# Revit family: Roller_Shades-Lutron-Wall_Mount-Roller_64
name_source: partatom
category: Specialty Equipment
revit_build: Autodesk Revit 2017 (Build: 20160720_1515(x64)
units: mm (PartAtom-declared; Revit-internal decimal feet)

## family parameters
Cut with Voids When Loaded = No
Host = Face
OmniClass Number = 23.30.60.14.21
OmniClass Title = Shades
Part Type = Normal
Room Calculation Point = No
Round Connector Dimension = Use Diameter
Shared = No

## types (4) — shared parameters
Assembly Code = E2010320
Default Elevation = 9' - 0"
Description = Motorized Roller Shade
Fabric Roll Detail = Standard
Instruction Sheet Link = http://www.lutron.com
Manufacturer = Lutron Electronics Co., Inc
Manufacturer Fax Number = 610-282-1243
Maximum Shade Area = 64.00 SF
Model = Roller 64
Performance URL = http://www.lutron.com
Product Documentation Link = http://www.lutron.com
Product Page URL = http://www.lutron.com
Series = Sivoia QS
Shade Material = Fabric - Lutron - Linen - White
URL = http://www.lutron.com
Version = 2017 - v1.0b
Video Link = https://www.youtube.com
Warranty URL = http://www.lutron.com
zero-valued in all types: Cost

## per-type parameters (varying)
| type | Mounting | No Pocket | Overall Depth | Pocket Mount Bracket Offset | Pocket Mount Enclosure | Product Name | Shade Symbol Offset |
| Roller 64 - Wall Mount | Wall | Yes | 0' - 3 9/32" | 0' - 0" | No | Roller 64 - Motorized Roller Shade - Wall Mount | 0' - 0 3/4" |
| Roller 64 - Inside Mount | Inside | Yes | 0' - 3 9/32" | 0' - 0" | No | Roller 64 - Motorized Roller Shade - Inside Mount | 0' - 0 3/4" |
| Roller 64 - Outside Mount | Outside | Yes | 0' - 3 9/32" | 0' - 0" | No | Roller 64 - Motorized Roller Shade - Outside Mount | 0' - 0 3/4" |
| Roller 64 - Pocket Mount | Pocket | No | 0' - 3 1/2" | 0' - 0 1/16" | Yes | Roller 64 - Motorized Roller Shade - Pocket Mount | 0' - 0" |

## geometry (parser evidence)
native form markers: Blend x3, Sweep x2
no freeform markers — native parametric forms only
